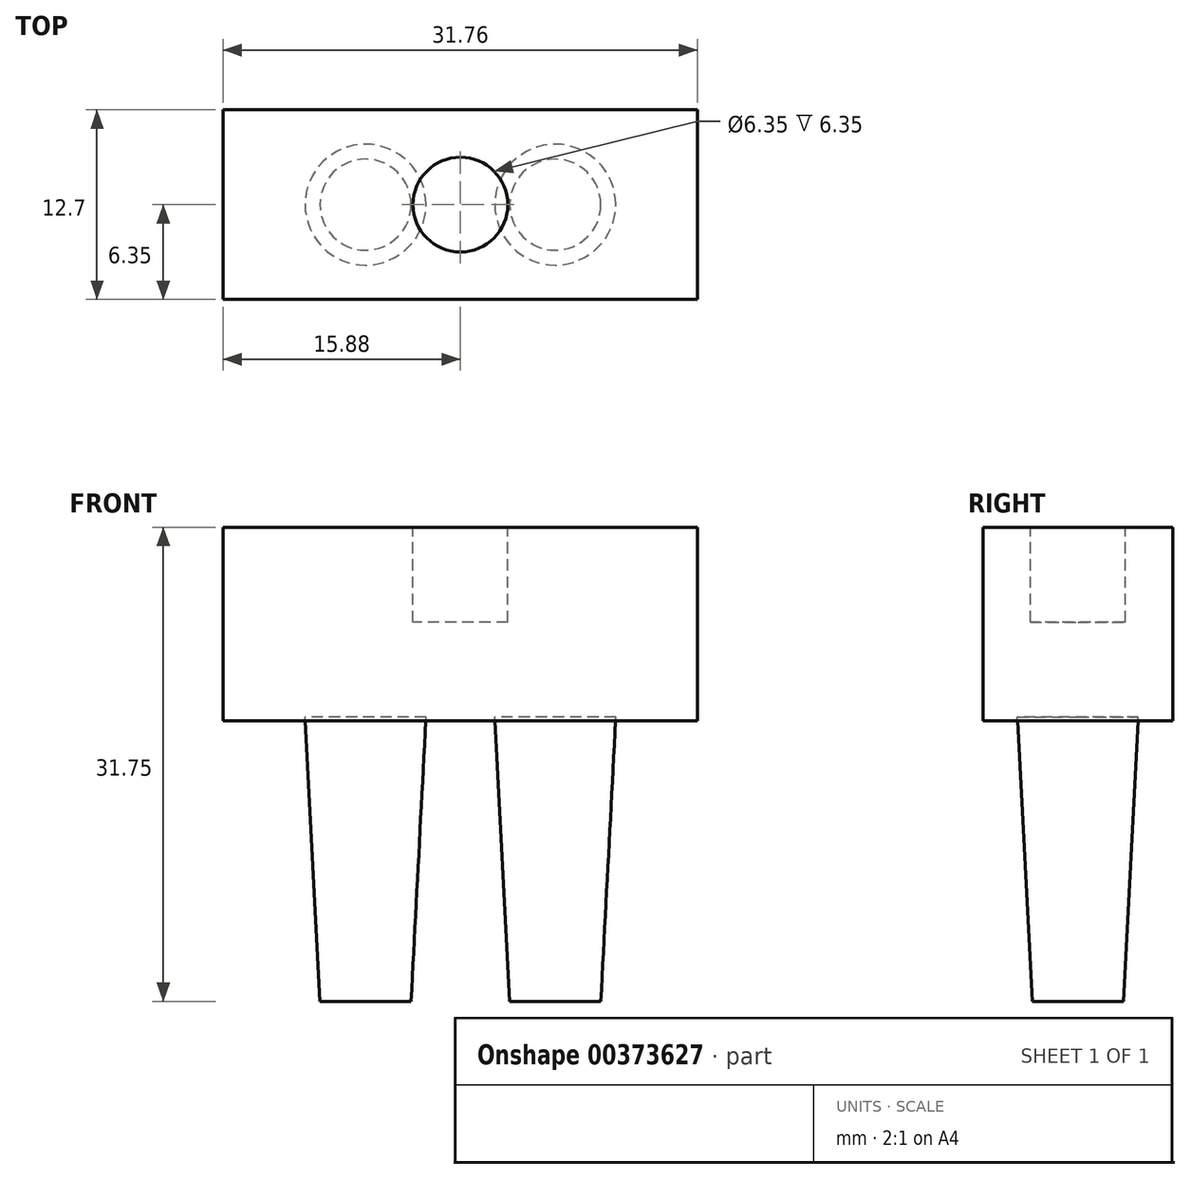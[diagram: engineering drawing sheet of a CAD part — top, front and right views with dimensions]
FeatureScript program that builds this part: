
annotation { "Feature Type Name" : "Feature", "Feature Type Description" : "" }
export const myFeature = defineFeature(function(context is Context, id is Id, definition is map)
    precondition{}
    {
        {
            var Q0;
            Q0=qCreatedBy(makeId("Top.planeOp"),FACE);
            var sketch = newSketch(context, id + "F0", { "sketchPlane" : qUnion([Q0])});
            skCircle(sketch, "E0", {"center": v(6.35, 0) * mm, "radius": 3.05 * mm});
            skCircle(sketch, "E1.MirrorC", {"center": v(-6.35, 0) * mm, "radius": 3.05 * mm});
            skSolve(sketch);
        }
        {
            var Q0;
            Q0 = qSketchRegion(id + "F0", true);
            extrude(context, id + "F1", {"entities" : qUnion([Q0]), "depth" : 19.05 * mm, "hasDraft" : true, "draftAngle" : 3 * degree});
        }
        {
            var Q0;
            Q0=makeQuery(id+"F1.opExtrude","CAP_FACE",FACE,{"disambiguationData":[OSD([sQuery(id+"F0.wireOp",EDGE,"E1.MirrorC")])],"isStart":false});
            var sketch = newSketch(context, id + "F2", { "sketchPlane" : qUnion([Q0])});
            skLineSegment(sketch, "E2.bottom", {"start": v(15.88, 6.35) * mm, "end": v(-15.88, 6.35) * mm});
            skLineSegment(sketch, "E2.top", {"start": v(15.88, -6.35) * mm, "end": v(-15.88, -6.35) * mm});
            skLineSegment(sketch, "E2.left", {"start": v(15.88, 6.35) * mm, "end": v(15.88, -6.35) * mm});
            skLineSegment(sketch, "E2.right", {"start": v(-15.88, 6.35) * mm, "end": v(-15.88, -6.35) * mm});
            skPoint(sketch, "E2.middle", {"position": v(0, 0) * mm});
            skSolve(sketch);
        }
        {
            var Q0;
            Q0 = qSketchRegion(id + "F2", true);
            extrude(context, id + "F3", {"entities" : qUnion([Q0]), "depth" : 12.7 * mm, "hasSecondDirection" : true, "secondDirectionOppositeDirection" : true, "secondDirectionDepth" : 0.25 * mm});
        }
        {
            var Q0;
            Q0=makeQuery(id+"F3.opExtrude","CAP_FACE",FACE,{"disambiguationData":[OSD([sQuery(id+"F2.wireOp",EDGE,"E2.bottom"),sQuery(id+"F2.wireOp",EDGE,"E2.top"),sQuery(id+"F2.wireOp",EDGE,"E2.left"),sQuery(id+"F2.wireOp",EDGE,"E2.right")])],"isStart":false});
            var sketch = newSketch(context, id + "F4", { "sketchPlane" : qUnion([Q0])});
            skCircle(sketch, "E3", {"center": v(0, 0) * mm, "radius": 3.18 * mm});
            skSolve(sketch);
        }
        {
            var Q0;
            Q0 = qSketchRegion(id + "F4", true);
            extrude(context, id + "F5", {"entities" : qUnion([Q0]), "operationType" : NewBodyOperationType.REMOVE, "oppositeDirection" : true, "depth" : 6.35 * mm});
        }
    });
